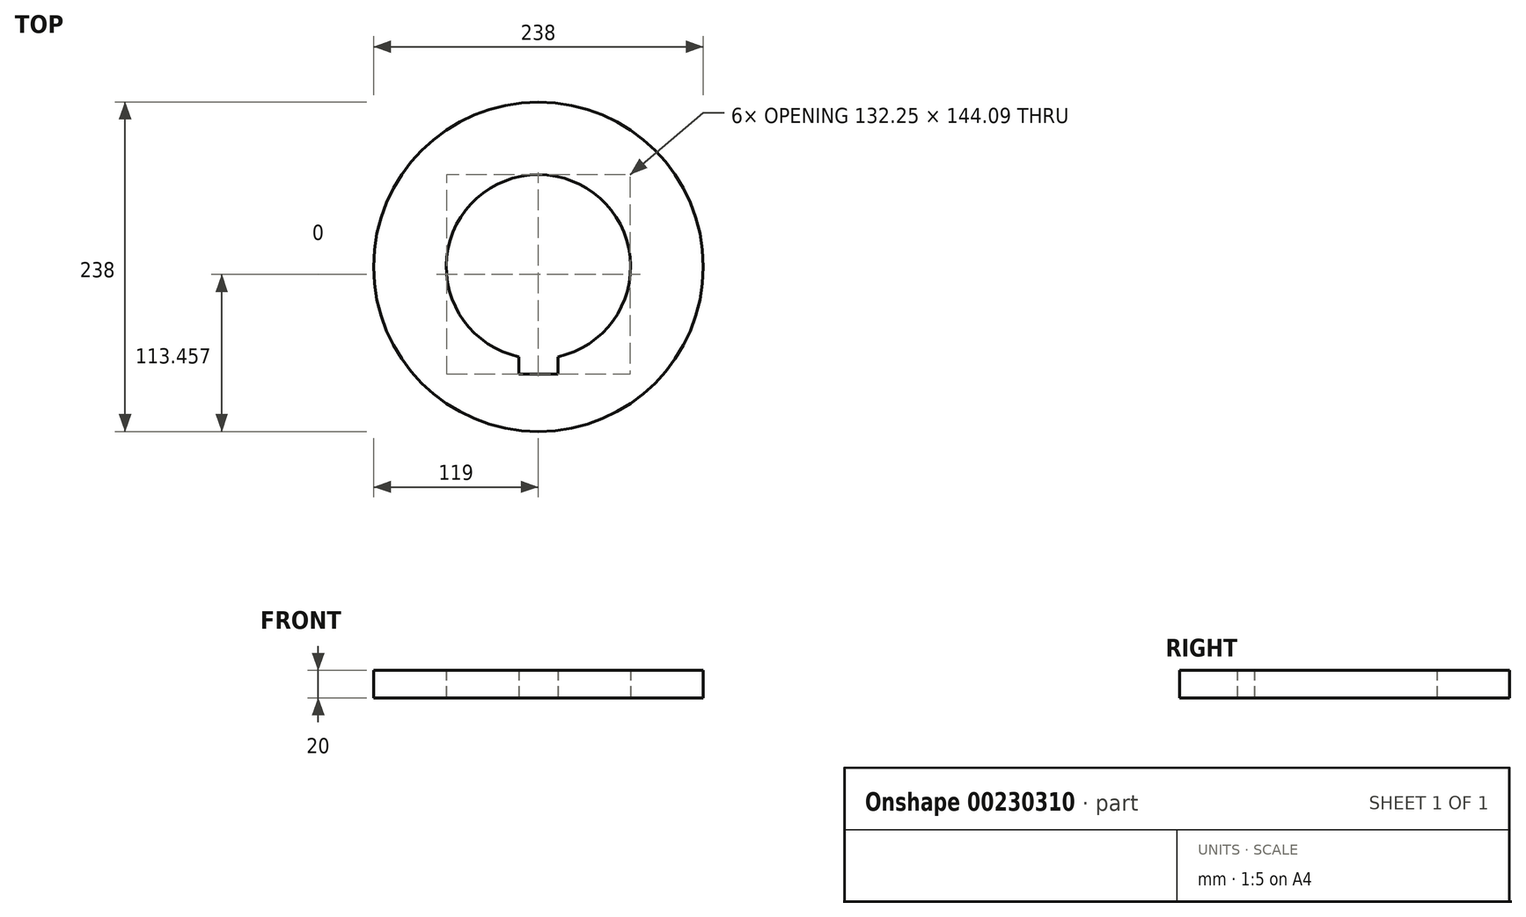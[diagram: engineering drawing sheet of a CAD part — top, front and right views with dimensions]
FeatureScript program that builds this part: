
annotation { "Feature Type Name" : "Feature", "Feature Type Description" : "" }
export const myFeature = defineFeature(function(context is Context, id is Id, definition is map)
    precondition{}
    {
        {
            var Q0;
            Q0=qCreatedBy(makeId("Top.planeOp"),FACE);
            var sketch = newSketch(context, id + "F0", { "sketchPlane" : qUnion([Q0])});
            skCircle(sketch, "E0", {"center": v(0, 0) * mm, "radius": 119 * mm});
            skCircle(sketch, "E1", {"center": v(0, 0) * mm, "radius": 70 * mm, "construction": true});
            skLineSegment(sketch, "E2", {"start": v(0, 0) * mm, "end": v(0, -89.94) * mm, "construction": true});
            skLineSegment(sketch, "E3.0", {"start": v(-14, -65) * mm, "end": v(-14, -77.59) * mm});
            skLineSegment(sketch, "E4.0", {"start": v(14, -65) * mm, "end": v(14, -77.59) * mm});
            skLineSegment(sketch, "E5", {"start": v(-14, -77.59) * mm, "end": v(14, -77.59) * mm});
            skLineSegment(sketch, "E6", {"start": v(0, 0) * mm, "end": v(0, 70) * mm});
            skCircle(sketch, "E7", {"center": v(0, 0) * mm, "radius": 115 * mm, "construction": true});
            skCircle(sketch, "E8", {"center": v(0, 0) * mm, "radius": 66.5 * mm});
            skSolve(sketch);
        }
        {
            var Q0;
            Q0=makeQuery(id+"F0.imprint","IMPRINT",FACE,{"disambiguationData":[TD([[makeQuery(id+"F0.imprint","IMPRINT",EDGE,{"derivedFrom":sQuery(id+"F0.wireOp",EDGE,"E0")}),1.0]])]});
            extrude(context, id + "F1", {"entities" : qUnion([Q0]), "depth" : 20 * mm});
        }
    });
